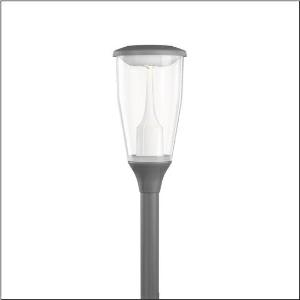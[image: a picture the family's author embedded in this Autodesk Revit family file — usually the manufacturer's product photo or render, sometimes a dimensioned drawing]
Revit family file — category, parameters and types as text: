
# Revit family: dl_11_iq___st1_2a_5xa5575kf14h000022_bb26
name_source: partatom
category: Lighting Fixtures
units: mm (PartAtom-declared; Revit-internal decimal feet)

## family parameters
Cut with Voids When Loaded = No
Host = Face
Light Source = No
Part Type = Normal
Room Calculation Point = No
Round Connector Dimension = Use Diameter
Shared = No

## types (1)
- --- (1 x LED, 1560 lm, 10 W, 4000K)
    Apparent Load = 10 VA
    CIE Flux Codes = 24 63 94 96 100
    Color Rendering = 70
    Color Temperature = 4000K
    Default Elevation = 1800 mm
    Description = DL 11 iQ, mast luminaire, Module 540 iQ-SR, primary light control with 3 zone facetted reflector, of plastic, silver coated, highly specular, structured, primary optical cover: cover, of PMMA, transparent, light distribution: ST1.2a, light emission: direct distribution, primary light characteristic: asymmetric, installation type: post-top, LED, High Power LED, light colour: 740, colour temperature: 4000K, control: Street-Remote, Auto-Match, Temp-Guard, Lumen-Switch, Night-Set, Smart-Wire, Light-Fading, Desk-Remote (wireless, voltage-free reading and setting of iQ features in the workshop via application-optimized NFC function/RFID function), optimised constant luminous flux control (CLO 2.0), mains connection: 220..240V, AC, 50/60Hz, connection cable pre-assembled, cable length: 5,5m, start of lifetime: 10W, end of service life: 10W, luminaire housing, upper part, of diecast aluminium, coated, Siteco® metallic grey (DB 702S), spigot size: 76mm (post-top), post-top mast mounting element, of diecast aluminium, coated, Siteco® metallic grey (DB 702S), Module 540 iQ-SR, traffic white (RAL 9016), equipment: standard, protection rating (complete): IP66, insulation class (complete): insulation class II (safety insulation), certification: CE, ENEC, ENEC+, VDE, packaging unit: 1 piece

Light Distribution: ST1.2a
    Height = 665 mm
    Lamp = 1 x LED
    Lamp Light Flux = 1560 lm
    Lamp Power = 10 W
    Lamp count = 1
    Length = 334 mm
    Luminous efficacy = 156 lm/W
    Manufacturer = Siteco
    ModVariant = No
    Model = 5XA5575KF14H000022
    Number of Poles = 1
    OnlyDefault = Yes
    Power Factor = 1
    Product Name = DL 11 iQ | ST1.2a
    Product group = mast luminaire | pylon top
    ProductGroupID = 6100
    Protection Class = Protection class II
    Protection Degree = IP 66
    RLX_Detail_Level = 1
    RLX_Emergency_Light_Flux = 0 lm
    RLX_Emergency_Type = 0
    RLX_Emergency_Type_DB = No
    RlxData = <blob elided: 157697 chars, md5=af77da88>
    Socket = socket
    Standby Power = 0 W
    System Light Flux = 1560 lm
    System Power = 10 W
    Type Comments = factory setting: luminous flux: 100 % | dim-lin: 254 | 401 mA
    Type Image = l_1258354.jpg
    URL = http://relux.com
    VarID = @adj_043899
    Voltage = 0 V
    Weight = 0.00 kg
    Width = 0 mm  [stored 0 ft]

note: [stored X ft] marks values corroborated as IEEE doubles in the binary element streams (Revit-internal decimal feet)

## geometry (parser evidence)
native form markers: Blend x4, Sweep x11
no freeform markers — native parametric forms only
